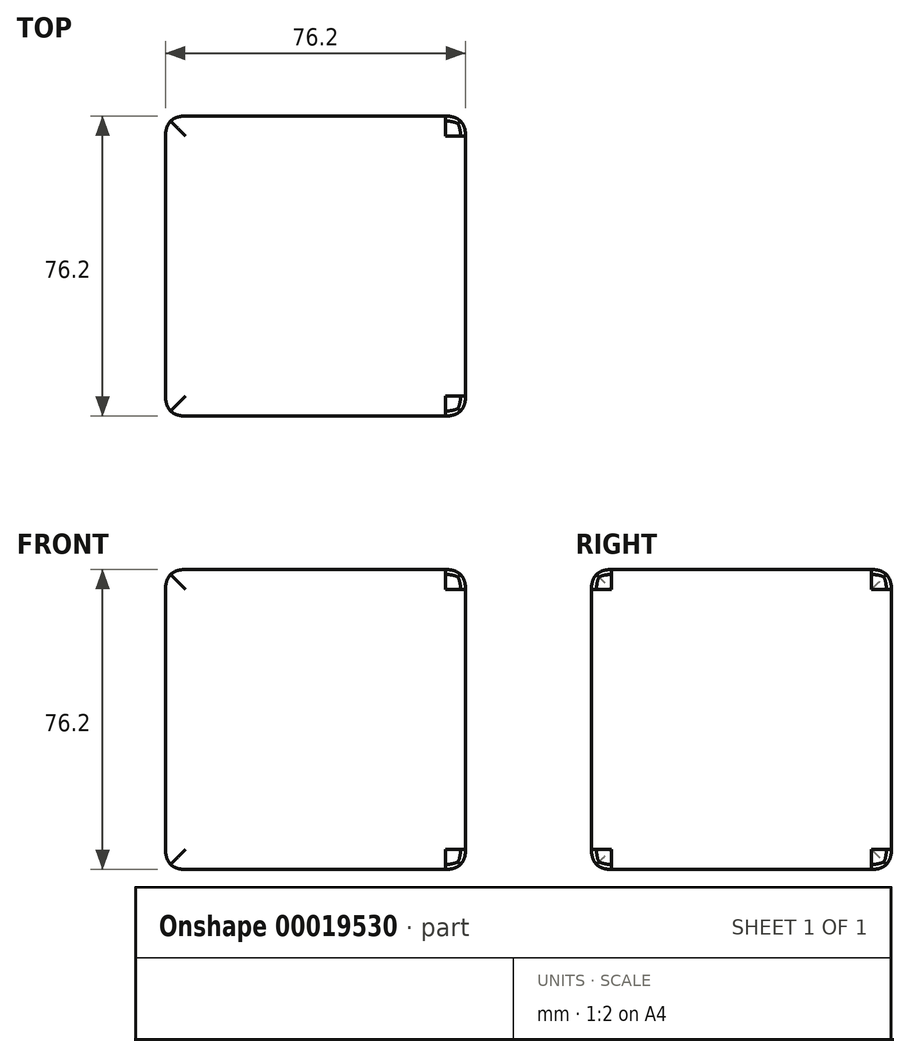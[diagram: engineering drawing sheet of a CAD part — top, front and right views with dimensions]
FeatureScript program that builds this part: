
annotation { "Feature Type Name" : "Feature", "Feature Type Description" : "" }
export const myFeature = defineFeature(function(context is Context, id is Id, definition is map)
    precondition{}
    {
        {
            var Q0;
            Q0=qCreatedBy(makeId("Top.planeOp"),FACE);
            var sketch = newSketch(context, id + "F0", { "sketchPlane" : qUnion([Q0])});
            skLineSegment(sketch, "E0.rect.bottom", {"start": v(38.1, 38.1) * mm, "end": v(-38.1, 38.1) * mm});
            skLineSegment(sketch, "E0.rect.top", {"start": v(38.1, -38.1) * mm, "end": v(-38.1, -38.1) * mm});
            skLineSegment(sketch, "E0.rect.left", {"start": v(38.1, 38.1) * mm, "end": v(38.1, -38.1) * mm});
            skLineSegment(sketch, "E0.rect.right", {"start": v(-38.1, 38.1) * mm, "end": v(-38.1, -38.1) * mm});
            skPoint(sketch, "E0.rect.middle", {"position": v(0, 0) * mm});
            skSolve(sketch);
        }
        {
            var Q0;
            Q0=makeQuery(id+"F0.imprint","IMPRINT",FACE,{"disambiguationData":[TD([[makeQuery(id+"F0.imprint","IMPRINT",EDGE,{"derivedFrom":sQuery(id+"F0.wireOp",EDGE,"E0.rect.bottom")}),1.0]])]});
            extrude(context, id + "F1", {"entities" : qUnion([Q0]), "depth" : 76.2 * mm});
        }
        {
            var Q0;
            Q0=makeQuery(id+"F1.opExtrude","SWEPT_EDGE",EDGE,{"disambiguationData":[OSD([sQuery(id+"F0.wireOp",EDGE,"E0.rect.bottom"),sQuery(id+"F0.wireOp",EDGE,"E0.rect.right")])]});
            var Q1;
            Q1=makeQuery(id+"F1.opExtrude","SWEPT_EDGE",EDGE,{"disambiguationData":[OSD([sQuery(id+"F0.wireOp",EDGE,"E0.rect.top"),sQuery(id+"F0.wireOp",EDGE,"E0.rect.right")])]});
            var Q2;
            Q2=makeQuery(id+"F1.opExtrude","CAP_EDGE",EDGE,{"disambiguationData":[OSD([sQuery(id+"F0.wireOp",EDGE,"E0.rect.right")])],"isStart":true});
            var Q3;
            Q3=makeQuery(id+"F1.opExtrude","CAP_EDGE",EDGE,{"disambiguationData":[OSD([sQuery(id+"F0.wireOp",EDGE,"E0.rect.right")])],"isStart":false});
            fillet(context, id + "F2", {"entities" : qUnion([Q0, Q1, Q2, Q3]), "radius" : 5.08 * mm, "rho" : 0.5, "crossSection" : FilletCrossSection.CONIC, "allowEdgeOverflow" : false});
        }
        {
            var Q0;
            Q0=makeQuery(id+"F1.opExtrude","SWEPT_FACE",FACE,{"disambiguationData":[OSD([sQuery(id+"F0.wireOp",EDGE,"E0.rect.top")])]});
            var Q1;
            Q1=makeQuery(id+"F1.opExtrude","SWEPT_EDGE",EDGE,{"disambiguationData":[OSD([sQuery(id+"F0.wireOp",EDGE,"E0.rect.top"),sQuery(id+"F0.wireOp",EDGE,"E0.rect.left")])]});
            var Q2;
            Q2=makeQuery(id+"F1.opExtrude","SWEPT_EDGE",EDGE,{"disambiguationData":[OSD([sQuery(id+"F0.wireOp",EDGE,"E0.rect.bottom"),sQuery(id+"F0.wireOp",EDGE,"E0.rect.left")])]});
            var Q3;
            Q3=makeQuery(id+"F1.opExtrude","CAP_FACE",FACE,{"disambiguationData":[OSD([sQuery(id+"F0.wireOp",EDGE,"E0.rect.bottom"),sQuery(id+"F0.wireOp",EDGE,"E0.rect.top"),sQuery(id+"F0.wireOp",EDGE,"E0.rect.left"),sQuery(id+"F0.wireOp",EDGE,"E0.rect.right")])],"isStart":true});
            var Q4;
            Q4=makeQuery(id+"F1.opExtrude","CAP_FACE",FACE,{"disambiguationData":[OSD([sQuery(id+"F0.wireOp",EDGE,"E0.rect.bottom"),sQuery(id+"F0.wireOp",EDGE,"E0.rect.top"),sQuery(id+"F0.wireOp",EDGE,"E0.rect.left"),sQuery(id+"F0.wireOp",EDGE,"E0.rect.right")])],"isStart":false});
            fillet(context, id + "F3", {"entities" : qUnion([Q0, Q1, Q2, Q3, Q4]), "radius" : 5.08 * mm, "rho" : 0.5, "crossSection" : FilletCrossSection.CONIC, "allowEdgeOverflow" : false});
        }
    });
